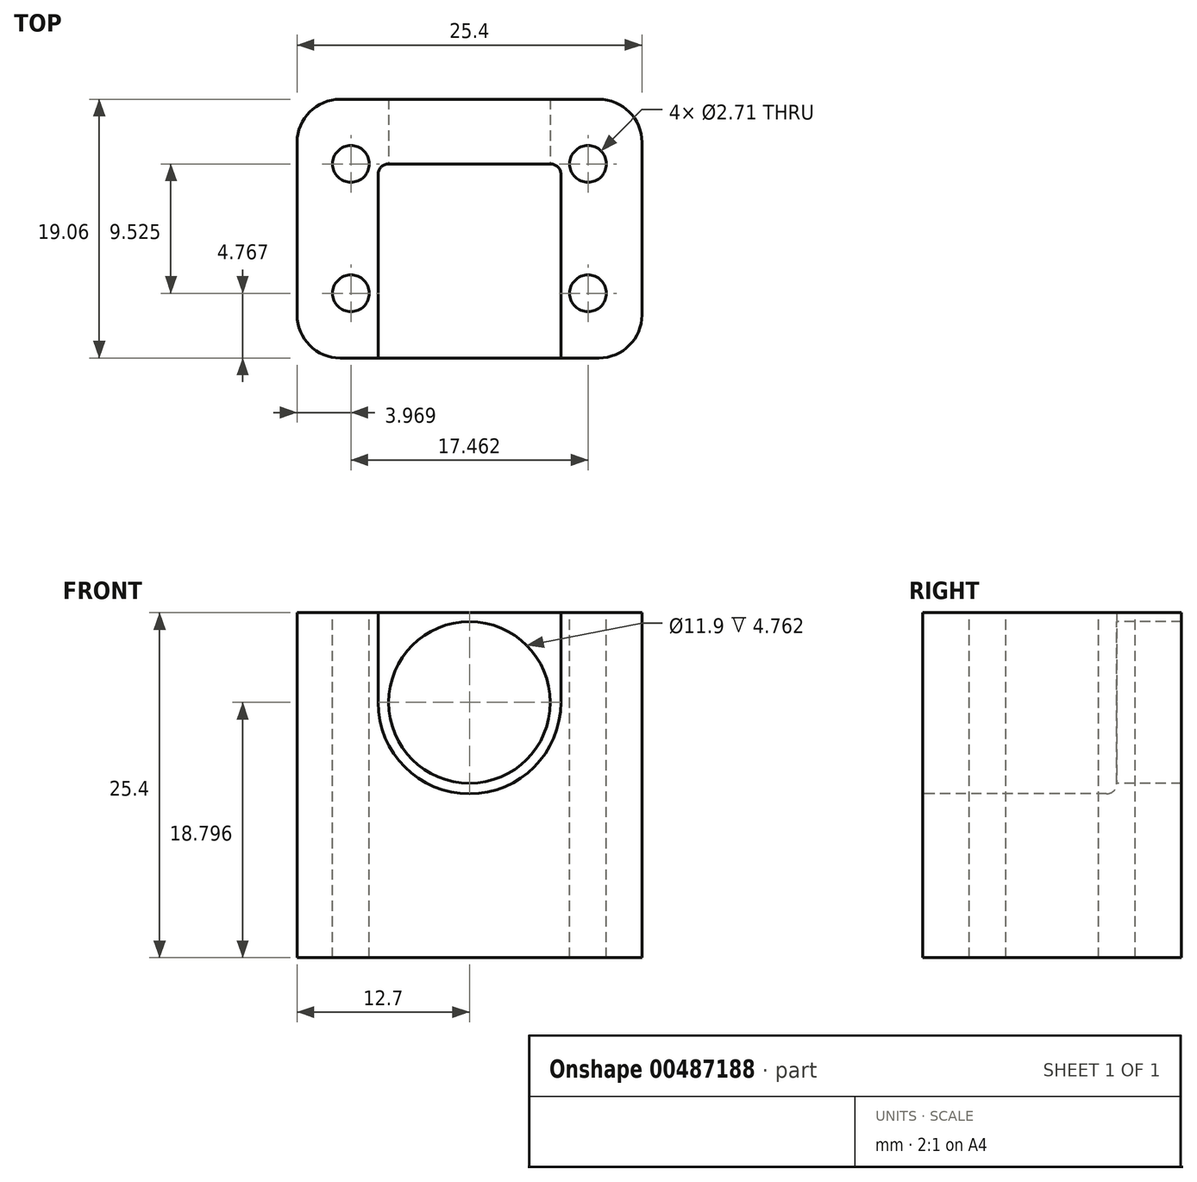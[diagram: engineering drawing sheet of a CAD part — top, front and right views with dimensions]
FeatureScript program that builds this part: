
annotation { "Feature Type Name" : "Feature", "Feature Type Description" : "" }
export const myFeature = defineFeature(function(context is Context, id is Id, definition is map)
    precondition{}
    {
        {
            var Q0;
            Q0=qCreatedBy(makeId("Top.planeOp"),FACE);
            var sketch = newSketch(context, id + "F0", { "sketchPlane" : qUnion([Q0])});
            skLineSegment(sketch, "E0.bottom", {"start": v(12.7, 9.53) * mm, "end": v(-12.7, 9.53) * mm});
            skLineSegment(sketch, "E0.top", {"start": v(12.7, -9.53) * mm, "end": v(-12.7, -9.53) * mm});
            skLineSegment(sketch, "E0.left", {"start": v(12.7, 9.53) * mm, "end": v(12.7, -9.53) * mm});
            skLineSegment(sketch, "E0.right", {"start": v(-12.7, 9.53) * mm, "end": v(-12.7, -9.53) * mm});
            skPoint(sketch, "E0.middle", {"position": v(0, 0) * mm});
            skSolve(sketch);
        }
        {
            var Q0;
            Q0=makeQuery(id+"F0.imprint","IMPRINT",FACE,{"disambiguationData":[TD([[makeQuery(id+"F0.imprint","IMPRINT",EDGE,{"derivedFrom":sQuery(id+"F0.wireOp",EDGE,"E0.bottom")}),1.0]])]});
            extrude(context, id + "F1", {"entities" : qUnion([Q0]), "depth" : 25.4 * mm});
        }
        {
            var Q0;
            Q0=makeQuery(id+"F1.opExtrude","SWEPT_FACE",FACE,{"disambiguationData":[OSD([sQuery(id+"F0.wireOp",EDGE,"E0.top")])]});
            var sketch = newSketch(context, id + "F2", { "sketchPlane" : qUnion([Q0])});
            skLineSegment(sketch, "E1", {"start": v(-6.73, 25.4) * mm, "end": v(-6.73, 18.8) * mm});
            skArc(sketch, "E2", {"start": v(-6.73, 18.8) * mm, "mid": v(0, 12.06) * mm, "end": v(6.73, 18.8) * mm});
            skLineSegment(sketch, "E3.MirrorCS", {"start": v(6.73, 25.4) * mm, "end": v(6.73, 18.8) * mm});
            skLineSegment(sketch, "E4.MirrorCS", {"start": v(-6.73, 25.4) * mm, "end": v(6.73, 25.4) * mm});
            skSolve(sketch);
        }
        {
            var Q0;
            Q0 = qSketchRegion(id + "F2", true);
            extrude(context, id + "F3", {"entities" : qUnion([Q0]), "operationType" : NewBodyOperationType.REMOVE, "oppositeDirection" : true, "depth" : 14.29 * mm});
        }
        {
            var Q0;
            Q0=makeQuery(id+"F1.opExtrude","CAP_FACE",FACE,{"disambiguationData":[OSD([sQuery(id+"F0.wireOp",EDGE,"E0.bottom"),sQuery(id+"F0.wireOp",EDGE,"E0.top"),sQuery(id+"F0.wireOp",EDGE,"E0.left"),sQuery(id+"F0.wireOp",EDGE,"E0.right")])],"isStart":false});
            var sketch = newSketch(context, id + "F4", { "sketchPlane" : qUnion([Q0])});
            skPoint(sketch, "E5", {"position": v(-8.73, 4.76) * mm});
            skPoint(sketch, "E6", {"position": v(-8.73, -4.76) * mm});
            skPoint(sketch, "E7", {"position": v(8.73, -4.76) * mm});
            skPoint(sketch, "E8", {"position": v(8.73, 4.76) * mm});
            skLineSegment(sketch, "E9", {"start": v(-8.73, 4.76) * mm, "end": v(-8.73, -4.76) * mm, "construction": true});
            skLineSegment(sketch, "E10", {"start": v(8.73, -4.76) * mm, "end": v(-8.73, -4.76) * mm, "construction": true});
            skLineSegment(sketch, "E11", {"start": v(0, -4.76) * mm, "end": v(0, 0) * mm, "construction": true});
            skLineSegment(sketch, "E12", {"start": v(-8.73, 0) * mm, "end": v(0, 0) * mm, "construction": true});
            skSolve(sketch);
        }
        {
            var Q0;
            Q0=sQuery(id+"F4.wireOp",VERTEX,"E5");
            var Q1;
            Q1=sQuery(id+"F4.wireOp",VERTEX,"E6");
            var Q2;
            Q2=sQuery(id+"F4.wireOp",VERTEX,"E8");
            var Q3;
            Q3=sQuery(id+"F4.wireOp",VERTEX,"E7");
            var Q4;
            Q4=makeQuery(id+"F1.opExtrude","SWEPT_BODY",BODY,{"disambiguationData":[OSD([sQuery(id+"F0.wireOp",EDGE,"E0.bottom"),sQuery(id+"F0.wireOp",EDGE,"E0.top"),sQuery(id+"F0.wireOp",EDGE,"E0.left"),sQuery(id+"F0.wireOp",EDGE,"E0.right")])]});
            hole(context, id + "F5", {"style" : HoleStyle.SIMPLE, "endStyle" : HoleEndStyle.THROUGH, "standardTappedOrClearance" : lookupTablePath({ "standard" : "ANSI", "engagement" : "75%", "pitch" : "32 tpi", "size" : "#6", "type" : "Tapped" }), "standardBlindInLast" : lookupTablePath({ "standard" : "ANSI", "engagement" : "75%", "pitch" : "32 tpi", "size" : "#6", "type" : "Tapped" }), "holeDiameter" : 2.7 * mm, "showTappedDepth" : true, "isTappedThrough" : true, "tappedDepth" : 12.7 * mm, "tapClearance" : 3, "locations" : qUnion([Q0, Q1, Q2, Q3]), "scope" : qUnion([Q4]), "majorDiameter" : 3.5 * mm});
        }
        {
            var Q0;
            Q0=makeQuery(id+"F3.boolean.opBoolean","COPY",FACE,{"derivedFrom":makeQuery(id+"F3.opExtrude","CAP_FACE",FACE,{"disambiguationData":[OSD([sQuery(id+"F2.wireOp",EDGE,"E1"),sQuery(id+"F2.wireOp",EDGE,"E2"),sQuery(id+"F2.wireOp",EDGE,"E3.MirrorCS"),sQuery(id+"F2.wireOp",EDGE,"E4.MirrorCS")])],"isStart":false})});
            var sketch = newSketch(context, id + "F6", { "sketchPlane" : qUnion([Q0])});
            skPoint(sketch, "E13", {"position": v(0, 18.8) * mm});
            skSolve(sketch);
        }
        {
            var Q0;
            Q0=sQuery(id+"F6.wireOp",VERTEX,"E13");
            var Q1;
            Q1=makeQuery(id+"F1.opExtrude","SWEPT_BODY",BODY,{"disambiguationData":[OSD([sQuery(id+"F0.wireOp",EDGE,"E0.bottom"),sQuery(id+"F0.wireOp",EDGE,"E0.top"),sQuery(id+"F0.wireOp",EDGE,"E0.left"),sQuery(id+"F0.wireOp",EDGE,"E0.right")])]});
            hole(context, id + "F7", {"style" : HoleStyle.SIMPLE, "endStyle" : HoleEndStyle.THROUGH, "standardTappedOrClearance" : lookupTablePath({ "standard" : "ANSI", "fit" : "Normal (ASME)", "size" : "7/16", "type" : "Clearance" }), "standardBlindInLast" : lookupTablePath({ "fit" : "Free", "standard" : "ANSI", "size" : "7/16", "type" : "Clearance" }), "holeDiameter" : 11.9 * mm, "isTappedThrough" : true, "tappedDepth" : 12.7 * mm, "tapClearance" : 3, "locations" : qUnion([Q0]), "scope" : qUnion([Q1])});
        }
        {
            var Q0;
            Q0=makeQuery(id+"F1.opExtrude","SWEPT_EDGE",EDGE,{"disambiguationData":[OSD([sQuery(id+"F0.wireOp",EDGE,"E0.top"),sQuery(id+"F0.wireOp",EDGE,"E0.right")])]});
            var Q1;
            Q1=makeQuery(id+"F1.opExtrude","SWEPT_EDGE",EDGE,{"disambiguationData":[OSD([sQuery(id+"F0.wireOp",EDGE,"E0.top"),sQuery(id+"F0.wireOp",EDGE,"E0.left")])]});
            var Q2;
            Q2=makeQuery(id+"F1.opExtrude","SWEPT_EDGE",EDGE,{"disambiguationData":[OSD([sQuery(id+"F0.wireOp",EDGE,"E0.bottom"),sQuery(id+"F0.wireOp",EDGE,"E0.left")])]});
            var Q3;
            Q3=makeQuery(id+"F1.opExtrude","SWEPT_EDGE",EDGE,{"disambiguationData":[OSD([sQuery(id+"F0.wireOp",EDGE,"E0.bottom"),sQuery(id+"F0.wireOp",EDGE,"E0.right")])]});
            fillet(context, id + "F8", {"entities" : qUnion([Q0, Q1, Q2, Q3]), "radius" : 3.17 * mm, "tangentPropagation" : true, "allowEdgeOverflow" : false});
        }
        {
            var Q0;
            Q0=makeQuery(id+"F3.boolean.opBoolean","COPY",EDGE,{"derivedFrom":makeQuery(id+"F3.opExtrude","CAP_EDGE",EDGE,{"disambiguationData":[OSD([sQuery(id+"F2.wireOp",EDGE,"E1")])],"isStart":false})});
            var Q1;
            Q1=makeQuery(id+"F3.boolean.opBoolean","COPY",EDGE,{"derivedFrom":makeQuery(id+"F3.opExtrude","CAP_EDGE",EDGE,{"disambiguationData":[OSD([sQuery(id+"F2.wireOp",EDGE,"E2")])],"isStart":false})});
            var Q2;
            Q2=makeQuery(id+"F3.boolean.opBoolean","COPY",EDGE,{"derivedFrom":makeQuery(id+"F3.opExtrude","CAP_EDGE",EDGE,{"disambiguationData":[OSD([sQuery(id+"F2.wireOp",EDGE,"E3.MirrorCS")])],"isStart":false})});
            fillet(context, id + "F9", {"entities" : qUnion([Q0, Q1, Q2]), "radius" : 0.76 * mm, "tangentPropagation" : true, "allowEdgeOverflow" : false});
        }
    });
